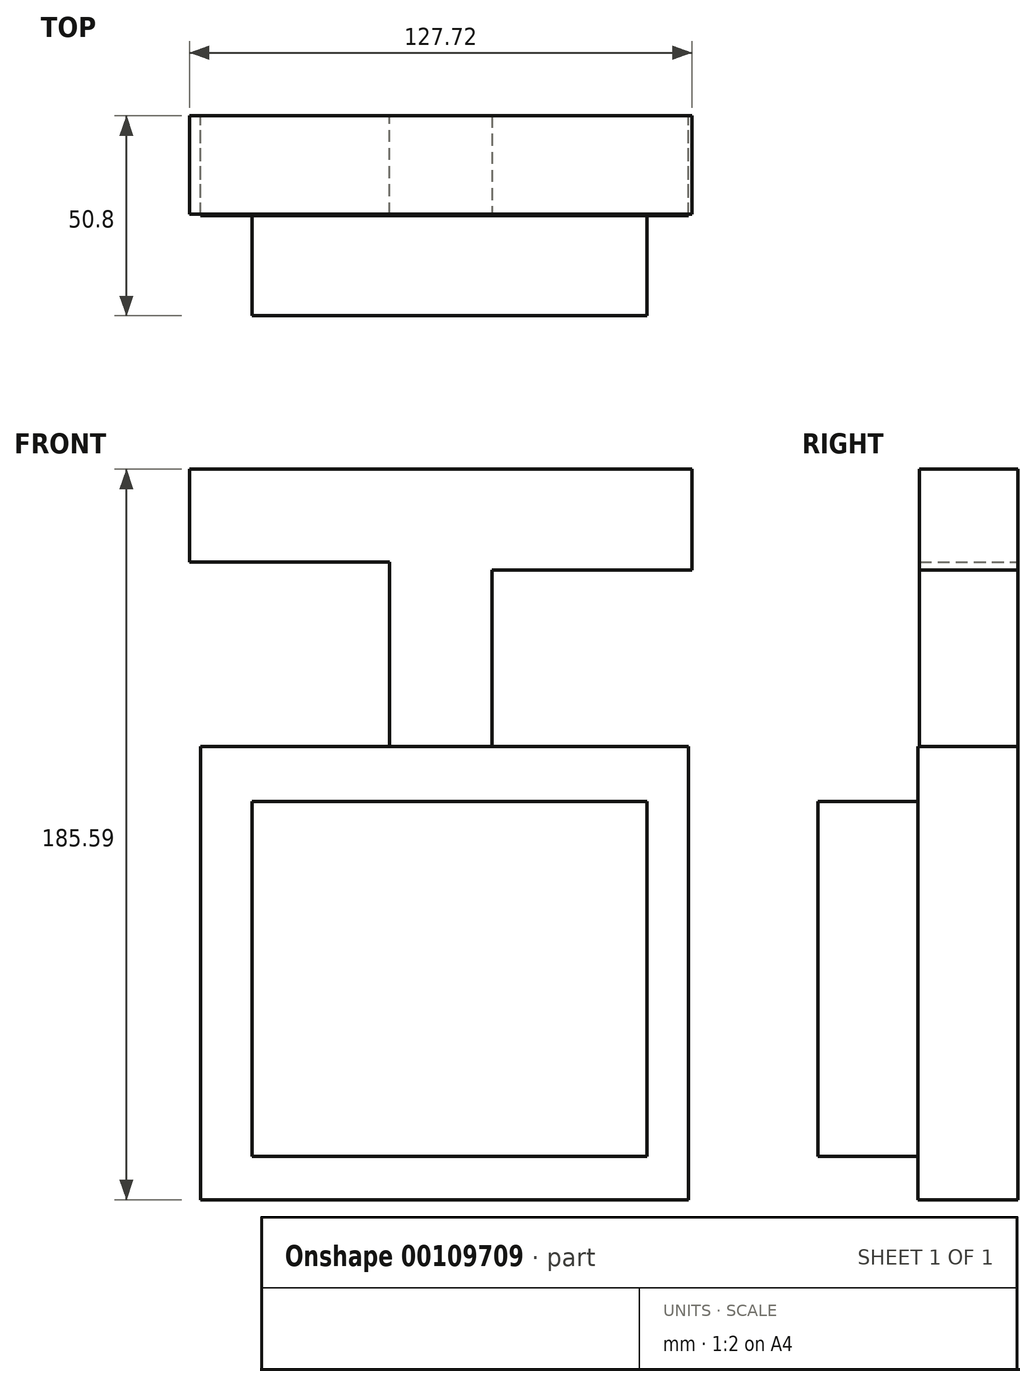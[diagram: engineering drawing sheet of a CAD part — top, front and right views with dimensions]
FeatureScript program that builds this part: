
annotation { "Feature Type Name" : "Feature", "Feature Type Description" : "" }
export const myFeature = defineFeature(function(context is Context, id is Id, definition is map)
    precondition{}
    {
        {
            var Q0;
            Q0=qCreatedBy(makeId("Front.planeOp"),FACE);
            var sketch = newSketch(context, id + "F0", { "sketchPlane" : qUnion([Q0])});
            skLineSegment(sketch, "E0.bottom", {"start": v(-62.35, 56.58) * mm, "end": v(61.6, 56.58) * mm});
            skLineSegment(sketch, "E0.top", {"start": v(-62.35, -58.6) * mm, "end": v(61.6, -58.6) * mm});
            skLineSegment(sketch, "E0.left", {"start": v(-62.35, 56.58) * mm, "end": v(-62.35, -58.6) * mm});
            skLineSegment(sketch, "E0.right", {"start": v(61.6, 56.58) * mm, "end": v(61.6, -58.6) * mm});
            skSolve(sketch);
        }
        {
            var Q0;
            Q0 = qSketchRegion(id + "F0", true);
            extrude(context, id + "F1", {"entities" : qUnion([Q0]), "depth" : 25.4 * mm});
        }
        {
            var Q0;
            Q0=qCreatedBy(makeId("Front.planeOp"),FACE);
            var sketch = newSketch(context, id + "F2", { "sketchPlane" : qUnion([Q0])});
            skLineSegment(sketch, "E1.bottom", {"start": v(-49.31, 42.59) * mm, "end": v(51.13, 42.59) * mm});
            skLineSegment(sketch, "E1.top", {"start": v(-49.31, -47.56) * mm, "end": v(51.13, -47.56) * mm});
            skLineSegment(sketch, "E1.left", {"start": v(-49.31, 42.59) * mm, "end": v(-49.31, -47.56) * mm});
            skLineSegment(sketch, "E1.right", {"start": v(51.13, 42.59) * mm, "end": v(51.13, -47.56) * mm});
            skSolve(sketch);
        }
        {
            var Q0;
            Q0 = qSketchRegion(id + "F2", true);
            extrude(context, id + "F3", {"entities" : qUnion([Q0]), "operationType" : NewBodyOperationType.ADD, "depth" : 50.8 * mm});
        }
        {
            var Q0;
            Q0=qCreatedBy(makeId("Top.planeOp"),FACE);
            var sketch = newSketch(context, id + "F4", { "sketchPlane" : qUnion([Q0])});
            skLineSegment(sketch, "E2.bottom", {"start": v(11.75, -25.01) * mm, "end": v(-14.37, -25.01) * mm});
            skLineSegment(sketch, "E2.top", {"start": v(11.75, 0) * mm, "end": v(-14.37, 0) * mm});
            skLineSegment(sketch, "E2.left", {"start": v(11.75, -25.01) * mm, "end": v(11.75, 0) * mm});
            skLineSegment(sketch, "E2.right", {"start": v(-14.37, -25.01) * mm, "end": v(-14.37, 0) * mm});
            skSolve(sketch);
        }
        {
            var Q0;
            Q0 = qSketchRegion(id + "F4", true);
            extrude(context, id + "F5", {"entities" : qUnion([Q0]), "operationType" : NewBodyOperationType.ADD, "depth" : 127 * mm});
        }
        {
            var Q0;
            Q0=makeQuery(id+"F5.opExtrude","SWEPT_FACE",FACE,{"disambiguationData":[OSD([sQuery(id+"F4.wireOp",EDGE,"E2.right")])]});
            var sketch = newSketch(context, id + "F6", { "sketchPlane" : qUnion([Q0])});
            skLineSegment(sketch, "E3.bottom", {"start": v(25.01, 127) * mm, "end": v(0, 127) * mm});
            skLineSegment(sketch, "E3.top", {"start": v(25.01, 103.43) * mm, "end": v(0, 103.43) * mm});
            skLineSegment(sketch, "E3.left", {"start": v(25.01, 127) * mm, "end": v(25.01, 103.43) * mm});
            skLineSegment(sketch, "E3.right", {"start": v(0, 127) * mm, "end": v(0, 103.43) * mm});
            skSolve(sketch);
        }
        {
            var Q0;
            Q0 = qSketchRegion(id + "F6", true);
            extrude(context, id + "F7", {"entities" : qUnion([Q0]), "operationType" : NewBodyOperationType.ADD, "depth" : 50.8 * mm});
        }
        {
            var Q0;
            Q0=makeQuery(id+"F5.opExtrude","SWEPT_FACE",FACE,{"disambiguationData":[OSD([sQuery(id+"F4.wireOp",EDGE,"E2.left")])]});
            var sketch = newSketch(context, id + "F8", { "sketchPlane" : qUnion([Q0])});
            skLineSegment(sketch, "E4.bottom", {"start": v(0, 127) * mm, "end": v(-25.01, 127) * mm});
            skLineSegment(sketch, "E4.top", {"start": v(0, 101.43) * mm, "end": v(-25.01, 101.43) * mm});
            skLineSegment(sketch, "E4.left", {"start": v(0, 127) * mm, "end": v(0, 101.43) * mm});
            skLineSegment(sketch, "E4.right", {"start": v(-25.01, 127) * mm, "end": v(-25.01, 101.43) * mm});
            skSolve(sketch);
        }
        {
            var Q0;
            Q0 = qSketchRegion(id + "F8", true);
            extrude(context, id + "F9", {"entities" : qUnion([Q0]), "operationType" : NewBodyOperationType.ADD, "depth" : 50.8 * mm});
        }
    });
